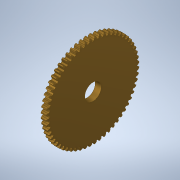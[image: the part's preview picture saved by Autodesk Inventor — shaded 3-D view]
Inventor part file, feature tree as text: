
AUTODESK INVENTOR PART (.ipt)
format: ipt  version: 2021 (Build 250183000, 183)  size: 605,184 bytes
history: native  units: mm
features: extrude x2, sketch x2, other x1, projected_geometry x1
ambient origin geometry x8: Origin, YZ Plane, XZ Plane, XY Plane, X Axis, Y Axis, Z Axis, Center Point
bodies: Body1 (feature_tree)
feature tree (6):
  other  "Sólido1"
  extrude  "Hole Machined"  Depth=10.0mm TaperAngle=0.0deg
  extrude  "Extrusion4"  [1 undecoded]
  sketch  "Sketch4"  dims[d17=5.5mm d18=10.0mm d19=0.0mm]
  sketch  "Sketch5"  dims[d21=10.0mm d22=0.0mm]
  projected_geometry  "Projected Loop1"
note: 1 required parameter value undecoded (feature->parameter linkage not recoverable at this tier; creation-order binding heuristic only, values carry confidence <= 0.55)
